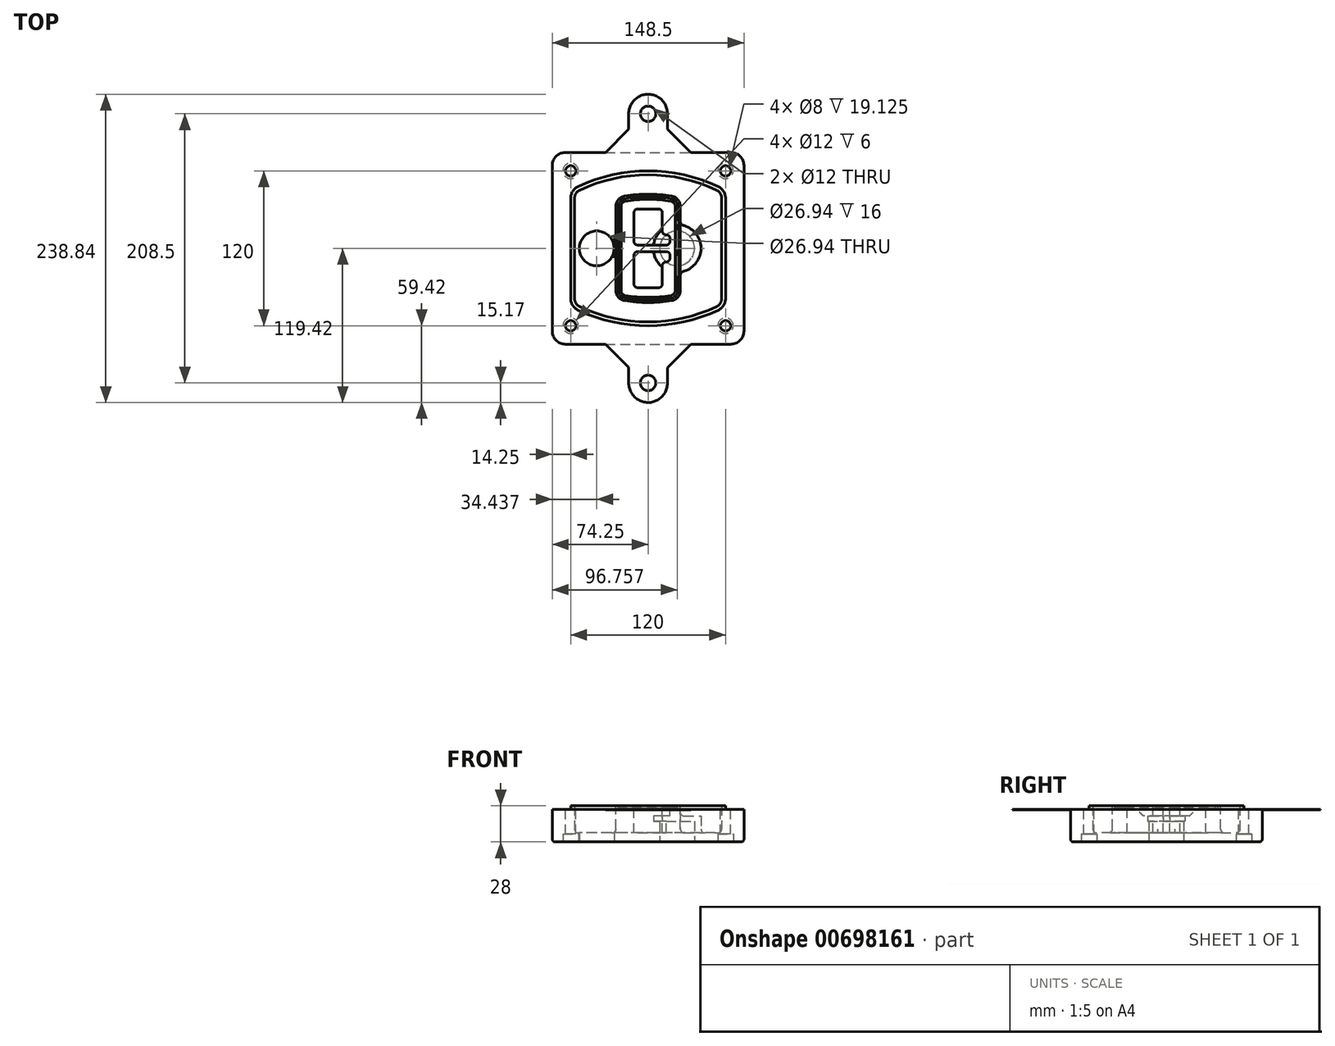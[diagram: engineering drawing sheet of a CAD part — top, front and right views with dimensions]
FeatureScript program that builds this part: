
annotation { "Feature Type Name" : "Feature", "Feature Type Description" : "" }
export const myFeature = defineFeature(function(context is Context, id is Id, definition is map)
    precondition{}
    {
        {
            var Q0;
            Q0=qCreatedBy(makeId("Top.planeOp"),FACE);
            var sketch = newSketch(context, id + "F0", { "sketchPlane" : qUnion([Q0])});
            skPoint(sketch, "E0.rect.middle", {"position": v(0, 0) * mm});
            skLineSegment(sketch, "E1.bottom", {"start": v(-64.25, -74.25) * mm, "end": v(64.25, -74.25) * mm});
            skLineSegment(sketch, "E1.top", {"start": v(-64.25, 74.25) * mm, "end": v(64.25, 74.25) * mm});
            skLineSegment(sketch, "E1.left", {"start": v(-74.25, -64.25) * mm, "end": v(-74.25, 64.25) * mm});
            skLineSegment(sketch, "E1.right", {"start": v(74.25, -64.25) * mm, "end": v(74.25, 64.25) * mm});
            skLineSegment(sketch, "E2", {"start": v(-74.25, 74.25) * mm, "end": v(74.25, -74.25) * mm, "construction": true});
            skLineSegment(sketch, "E3", {"start": v(74.25, 74.25) * mm, "end": v(-74.25, -74.25) * mm, "construction": true});
            skCircle(sketch, "E4", {"center": v(-60, 60) * mm, "radius": 4 * mm});
            skCircle(sketch, "E5", {"center": v(60, 60) * mm, "radius": 4 * mm});
            skCircle(sketch, "E6", {"center": v(60, -60) * mm, "radius": 4 * mm});
            skCircle(sketch, "E7", {"center": v(-60, -60) * mm, "radius": 4 * mm});
            skLineSegment(sketch, "E8", {"start": v(-60, 60) * mm, "end": v(60, 60) * mm, "construction": true});
            skLineSegment(sketch, "E9", {"start": v(60, 60) * mm, "end": v(60, -60) * mm, "construction": true});
            skLineSegment(sketch, "E10", {"start": v(60, -60) * mm, "end": v(-60, -60) * mm, "construction": true});
            skLineSegment(sketch, "E11", {"start": v(-60, -60) * mm, "end": v(-60, 60) * mm, "construction": true});
            skLineSegment(sketch, "E12", {"start": v(-60, 38.83) * mm, "end": v(-60, -38.83) * mm});
            skLineSegment(sketch, "E13", {"start": v(60, 38.83) * mm, "end": v(60, -38.83) * mm});
            skArc(sketch, "E14", {"start": v(54.26, 47.88) * mm, "mid": v(0, 60) * mm, "end": v(-54.26, 47.88) * mm});
            skArc(sketch, "E15", {"start": v(-54.26, -47.88) * mm, "mid": v(0, -60) * mm, "end": v(54.26, -47.88) * mm});
            skLineSegment(sketch, "E16", {"start": v(-60, 0) * mm, "end": v(60, 0) * mm, "construction": true});
            skPoint(sketch, "E17.visualSharp", {"position": v(-60, -45) * mm});
            skArc(sketch, "E17.filletArc", {"start": v(-60, -38.83) * mm, "mid": v(-58.44, -44.2) * mm, "end": v(-54.26, -47.88) * mm});
            skPoint(sketch, "E18.visualSharp", {"position": v(-60, 45) * mm});
            skArc(sketch, "E18.filletArc", {"start": v(-54.26, 47.88) * mm, "mid": v(-58.44, 44.2) * mm, "end": v(-60, 38.83) * mm});
            skPoint(sketch, "E19.visualSharp", {"position": v(60, 45) * mm});
            skArc(sketch, "E19.filletArc", {"start": v(60, 38.83) * mm, "mid": v(58.44, 44.2) * mm, "end": v(54.26, 47.88) * mm});
            skPoint(sketch, "E20.visualSharp", {"position": v(60, -45) * mm});
            skArc(sketch, "E20.filletArc", {"start": v(54.26, -47.88) * mm, "mid": v(58.44, -44.2) * mm, "end": v(60, -38.83) * mm});
            skPoint(sketch, "E21.visualSharp", {"position": v(-74.25, 74.25) * mm});
            skArc(sketch, "E21.filletArc", {"start": v(-64.25, 74.25) * mm, "mid": v(-71.32, 71.32) * mm, "end": v(-74.25, 64.25) * mm});
            skPoint(sketch, "E22.visualSharp", {"position": v(74.25, 74.25) * mm});
            skArc(sketch, "E22.filletArc", {"start": v(74.25, 64.25) * mm, "mid": v(71.32, 71.32) * mm, "end": v(64.25, 74.25) * mm});
            skPoint(sketch, "E23.visualSharp", {"position": v(74.25, -74.25) * mm});
            skArc(sketch, "E23.filletArc", {"start": v(64.25, -74.25) * mm, "mid": v(71.32, -71.32) * mm, "end": v(74.25, -64.25) * mm});
            skPoint(sketch, "E24.visualSharp", {"position": v(-74.25, -74.25) * mm});
            skArc(sketch, "E24.filletArc", {"start": v(-74.25, -64.25) * mm, "mid": v(-71.32, -71.32) * mm, "end": v(-64.25, -74.25) * mm});
            skArc(sketch, "E25.0", {"start": v(57, 38.83) * mm, "mid": v(55.9, 42.58) * mm, "end": v(52.98, 45.17) * mm});
            skLineSegment(sketch, "E25.1", {"start": v(57, 38.83) * mm, "end": v(57, -38.83) * mm});
            skArc(sketch, "E25.2", {"start": v(52.98, -45.17) * mm, "mid": v(55.9, -42.58) * mm, "end": v(57, -38.83) * mm});
            skArc(sketch, "E25.3", {"start": v(-52.98, -45.17) * mm, "mid": v(0, -57) * mm, "end": v(52.98, -45.17) * mm});
            skArc(sketch, "E25.4", {"start": v(-57, -38.83) * mm, "mid": v(-55.9, -42.58) * mm, "end": v(-52.98, -45.17) * mm});
            skArc(sketch, "E25.5", {"start": v(52.98, 45.17) * mm, "mid": v(0, 57) * mm, "end": v(-52.98, 45.17) * mm});
            skLineSegment(sketch, "E25.6", {"start": v(-57, 38.83) * mm, "end": v(-57, -38.83) * mm});
            skArc(sketch, "E25.7", {"start": v(-52.98, 45.17) * mm, "mid": v(-55.9, 42.58) * mm, "end": v(-57, 38.83) * mm});
            skArc(sketch, "E26.0", {"start": v(-55.96, 51.5) * mm, "mid": v(-61.82, 46.33) * mm, "end": v(-64, 38.83) * mm});
            skArc(sketch, "E26.1", {"start": v(55.96, 51.5) * mm, "mid": v(0, 64) * mm, "end": v(-55.96, 51.5) * mm});
            skArc(sketch, "E26.2", {"start": v(64, 38.83) * mm, "mid": v(61.82, 46.33) * mm, "end": v(55.96, 51.5) * mm});
            skLineSegment(sketch, "E26.3", {"start": v(64, 38.83) * mm, "end": v(64, -38.83) * mm});
            skArc(sketch, "E26.4", {"start": v(55.96, -51.5) * mm, "mid": v(61.82, -46.33) * mm, "end": v(64, -38.83) * mm});
            skLineSegment(sketch, "E26.5", {"start": v(-64, 38.83) * mm, "end": v(-64, -38.83) * mm});
            skArc(sketch, "E26.6", {"start": v(-55.96, -51.5) * mm, "mid": v(0, -64) * mm, "end": v(55.96, -51.5) * mm});
            skArc(sketch, "E26.7", {"start": v(-64, -38.83) * mm, "mid": v(-61.82, -46.33) * mm, "end": v(-55.96, -51.5) * mm});
            skSolve(sketch);
        }
        {
            var Q0;
            Q0=makeQuery(id+"F0.imprint","IMPRINT",FACE,{"disambiguationData":[TD([[makeQuery(id+"F0.imprint","IMPRINT",EDGE,{"derivedFrom":sQuery(id+"F0.wireOp",EDGE,"E1.bottom")}),1.0]])]});
            var Q1;
            Q1=makeQuery(id+"F0.imprint","IMPRINT",FACE,{"disambiguationData":[TD([[makeQuery(id+"F0.imprint","IMPRINT",EDGE,{"derivedFrom":sQuery(id+"F0.wireOp",EDGE,"E12")}),1.0]])]});
            var Q2;
            Q2=makeQuery(id+"F0.imprint","IMPRINT",FACE,{"disambiguationData":[TD([[makeQuery(id+"F0.imprint","IMPRINT",EDGE,{"derivedFrom":sQuery(id+"F0.wireOp",EDGE,"E25.0")}),1.0]])]});
            var Q3;
            Q3=makeQuery(id+"F0.imprint","IMPRINT",FACE,{"disambiguationData":[TD([[makeQuery(id+"F0.imprint","IMPRINT",EDGE,{"derivedFrom":sQuery(id+"F0.wireOp",EDGE,"E12")}),-1.0]])]});
            extrude(context, id + "F1", {"entities" : qUnion([Q0, Q1, Q2, Q3]), "oppositeDirection" : true, "depth" : 25 * mm});
        }
        {
            var Q0;
            Q0=makeQuery(id+"F0.imprint","IMPRINT",FACE,{"disambiguationData":[TD([[makeQuery(id+"F0.imprint","IMPRINT",EDGE,{"derivedFrom":sQuery(id+"F0.wireOp",EDGE,"E12")}),1.0]])]});
            extrude(context, id + "F2", {"entities" : qUnion([Q0]), "operationType" : NewBodyOperationType.ADD, "depth" : 3 * mm});
        }
        {
            var Q0;
            Q0=makeQuery(id+"F0.imprint","IMPRINT",FACE,{"disambiguationData":[TD([[makeQuery(id+"F0.imprint","IMPRINT",EDGE,{"derivedFrom":sQuery(id+"F0.wireOp",EDGE,"E25.0")}),1.0]])]});
            extrude(context, id + "F3", {"entities" : qUnion([Q0]), "operationType" : NewBodyOperationType.REMOVE, "oppositeDirection" : true, "depth" : 18 * mm});
        }
        {
            var Q0;
            Q0=makeQuery(id+"F2.opExtrude","CAP_FACE",FACE,{"disambiguationData":[OSD([sQuery(id+"F0.wireOp",EDGE,"E12"),sQuery(id+"F0.wireOp",EDGE,"E13"),sQuery(id+"F0.wireOp",EDGE,"E14"),sQuery(id+"F0.wireOp",EDGE,"E15"),sQuery(id+"F0.wireOp",EDGE,"E17.filletArc"),sQuery(id+"F0.wireOp",EDGE,"E18.filletArc"),sQuery(id+"F0.wireOp",EDGE,"E19.filletArc"),sQuery(id+"F0.wireOp",EDGE,"E20.filletArc"),sQuery(id+"F0.wireOp",EDGE,"E25.0"),sQuery(id+"F0.wireOp",EDGE,"E25.1"),sQuery(id+"F0.wireOp",EDGE,"E25.2"),sQuery(id+"F0.wireOp",EDGE,"E25.3"),sQuery(id+"F0.wireOp",EDGE,"E25.4"),sQuery(id+"F0.wireOp",EDGE,"E25.5"),sQuery(id+"F0.wireOp",EDGE,"E25.6"),sQuery(id+"F0.wireOp",EDGE,"E25.7")])],"isStart":false});
            var sketch = newSketch(context, id + "F4", { "sketchPlane" : qUnion([Q0])});
            skArc(sketch, "E27.0", {"start": v(-18.34, -40.45) * mm, "mid": v(0, -42) * mm, "end": v(18.34, -40.45) * mm});
            skArc(sketch, "E28.0", {"start": v(18.34, 40.45) * mm, "mid": v(0, 42) * mm, "end": v(-18.34, 40.45) * mm});
            skLineSegment(sketch, "E29", {"start": v(-25, 32.57) * mm, "end": v(-25, -32.57) * mm});
            skLineSegment(sketch, "E30", {"start": v(25, 32.57) * mm, "end": v(25, -32.57) * mm});
            skLineSegment(sketch, "E31", {"start": v(-25, 39.1) * mm, "end": v(25, 39.1) * mm, "construction": true});
            skLineSegment(sketch, "E32", {"start": v(-25, -39.1) * mm, "end": v(25, -39.1) * mm, "construction": true});
            skPoint(sketch, "E33.visualSharp", {"position": v(-25, 39.1) * mm});
            skArc(sketch, "E33.filletArc", {"start": v(-18.34, 40.45) * mm, "mid": v(-23.11, 37.73) * mm, "end": v(-25, 32.57) * mm});
            skPoint(sketch, "E34.visualSharp", {"position": v(25, 39.1) * mm});
            skArc(sketch, "E34.filletArc", {"start": v(25, 32.57) * mm, "mid": v(23.11, 37.73) * mm, "end": v(18.34, 40.45) * mm});
            skPoint(sketch, "E35.visualSharp", {"position": v(25, -39.1) * mm});
            skArc(sketch, "E35.filletArc", {"start": v(18.34, -40.45) * mm, "mid": v(23.11, -37.73) * mm, "end": v(25, -32.57) * mm});
            skPoint(sketch, "E36.visualSharp", {"position": v(-25, -39.1) * mm});
            skArc(sketch, "E36.filletArc", {"start": v(-25, -32.57) * mm, "mid": v(-23.11, -37.73) * mm, "end": v(-18.34, -40.45) * mm});
            skArc(sketch, "E37.0", {"start": v(52.98, 45.17) * mm, "mid": v(0, 57) * mm, "end": v(-52.98, 45.17) * mm});
            skArc(sketch, "E37.1", {"start": v(-52.98, 45.17) * mm, "mid": v(-55.9, 42.58) * mm, "end": v(-57, 38.83) * mm});
            skLineSegment(sketch, "E37.2", {"start": v(-57, 38.83) * mm, "end": v(-57, -38.83) * mm});
            skArc(sketch, "E37.3", {"start": v(-57, -38.83) * mm, "mid": v(-55.9, -42.58) * mm, "end": v(-52.98, -45.17) * mm});
            skArc(sketch, "E37.4", {"start": v(-52.98, -45.17) * mm, "mid": v(0, -57) * mm, "end": v(52.98, -45.17) * mm});
            skArc(sketch, "E37.5", {"start": v(52.98, -45.17) * mm, "mid": v(55.9, -42.58) * mm, "end": v(57, -38.83) * mm});
            skLineSegment(sketch, "E37.6", {"start": v(57, 38.83) * mm, "end": v(57, -38.83) * mm});
            skArc(sketch, "E37.7", {"start": v(57, 38.83) * mm, "mid": v(55.9, 42.58) * mm, "end": v(52.98, 45.17) * mm});
            skLineSegment(sketch, "E38.0", {"start": v(23, 32.57) * mm, "end": v(23, -32.57) * mm});
            skArc(sketch, "E38.1", {"start": v(18, -38.48) * mm, "mid": v(21.58, -36.44) * mm, "end": v(23, -32.57) * mm});
            skArc(sketch, "E38.2", {"start": v(-18, -38.48) * mm, "mid": v(0, -40) * mm, "end": v(18, -38.48) * mm});
            skArc(sketch, "E38.3", {"start": v(-23, -32.57) * mm, "mid": v(-21.58, -36.44) * mm, "end": v(-18, -38.48) * mm});
            skLineSegment(sketch, "E38.4", {"start": v(-23, 32.57) * mm, "end": v(-23, -32.57) * mm});
            skArc(sketch, "E38.5", {"start": v(23, 32.57) * mm, "mid": v(21.58, 36.44) * mm, "end": v(18, 38.48) * mm});
            skArc(sketch, "E38.6", {"start": v(-18, 38.48) * mm, "mid": v(-21.58, 36.44) * mm, "end": v(-23, 32.57) * mm});
            skArc(sketch, "E38.7", {"start": v(18, 38.48) * mm, "mid": v(0, 40) * mm, "end": v(-18, 38.48) * mm});
            skArc(sketch, "E39.0", {"start": v(21, 32.57) * mm, "mid": v(20.06, 35.15) * mm, "end": v(17.67, 36.5) * mm});
            skLineSegment(sketch, "E39.1", {"start": v(21, 32.57) * mm, "end": v(21, -32.57) * mm});
            skArc(sketch, "E39.2", {"start": v(17.67, -36.5) * mm, "mid": v(20.06, -35.15) * mm, "end": v(21, -32.57) * mm});
            skArc(sketch, "E39.3", {"start": v(-17.67, -36.5) * mm, "mid": v(0, -38) * mm, "end": v(17.67, -36.5) * mm});
            skArc(sketch, "E39.4", {"start": v(-21, -32.57) * mm, "mid": v(-20.06, -35.15) * mm, "end": v(-17.67, -36.5) * mm});
            skArc(sketch, "E39.5", {"start": v(17.67, 36.5) * mm, "mid": v(0, 38) * mm, "end": v(-17.67, 36.5) * mm});
            skLineSegment(sketch, "E39.6", {"start": v(-21, 32.57) * mm, "end": v(-21, -32.57) * mm});
            skArc(sketch, "E39.7", {"start": v(-17.67, 36.5) * mm, "mid": v(-20.06, 35.15) * mm, "end": v(-21, 32.57) * mm});
            skLineSegment(sketch, "E40", {"start": v(-25, 0) * mm, "end": v(25, 0) * mm, "construction": true});
            skLineSegment(sketch, "E41", {"start": v(-11, 5.5) * mm, "end": v(-11, 27.5) * mm});
            skLineSegment(sketch, "E42", {"start": v(-8, 30.5) * mm, "end": v(8, 30.5) * mm});
            skLineSegment(sketch, "E43", {"start": v(11, 27.5) * mm, "end": v(11, 13.5) * mm});
            skLineSegment(sketch, "E44", {"start": v(14, 10.5) * mm, "end": v(14, 10.5) * mm});
            skLineSegment(sketch, "E45", {"start": v(17, 7.5) * mm, "end": v(17, 5.5) * mm});
            skLineSegment(sketch, "E46", {"start": v(14, 2.5) * mm, "end": v(-8, 2.5) * mm});
            skPoint(sketch, "E47.visualSharp", {"position": v(-11, 30.5) * mm});
            skArc(sketch, "E47.filletArc", {"start": v(-8, 30.5) * mm, "mid": v(-10.12, 29.62) * mm, "end": v(-11, 27.5) * mm});
            skPoint(sketch, "E48.visualSharp", {"position": v(11, 30.5) * mm});
            skArc(sketch, "E48.filletArc", {"start": v(11, 27.5) * mm, "mid": v(10.12, 29.62) * mm, "end": v(8, 30.5) * mm});
            skPoint(sketch, "E49.visualSharp", {"position": v(11, 10.5) * mm});
            skArc(sketch, "E49.filletArc", {"start": v(11, 13.5) * mm, "mid": v(11.88, 11.38) * mm, "end": v(14, 10.5) * mm});
            skPoint(sketch, "E50.visualSharp", {"position": v(17, 10.5) * mm});
            skArc(sketch, "E50.filletArc", {"start": v(17, 7.5) * mm, "mid": v(16.12, 9.62) * mm, "end": v(14, 10.5) * mm});
            skPoint(sketch, "E51.visualSharp", {"position": v(17, 2.5) * mm});
            skArc(sketch, "E51.filletArc", {"start": v(14, 2.5) * mm, "mid": v(16.12, 3.38) * mm, "end": v(17, 5.5) * mm});
            skPoint(sketch, "E52.visualSharp", {"position": v(-11, 2.5) * mm});
            skArc(sketch, "E52.filletArc", {"start": v(-11, 5.5) * mm, "mid": v(-10.12, 3.38) * mm, "end": v(-8, 2.5) * mm});
            skLineSegment(sketch, "E53.0.MirrorCS", {"start": v(14, -2.5) * mm, "end": v(-8, -2.5) * mm});
            skArc(sketch, "E54.0.MirrorCS", {"start": v(-11, -5.5) * mm, "mid": v(-10.12, -3.38) * mm, "end": v(-8, -2.5) * mm});
            skLineSegment(sketch, "E55.0.MirrorCS", {"start": v(-11, -5.5) * mm, "end": v(-11, -27.5) * mm});
            skArc(sketch, "E56.0.MirrorCS", {"start": v(-8, -30.5) * mm, "mid": v(-10.12, -29.62) * mm, "end": v(-11, -27.5) * mm});
            skLineSegment(sketch, "E57.0.MirrorCS", {"start": v(-8, -30.5) * mm, "end": v(8, -30.5) * mm});
            skArc(sketch, "E58.0.MirrorCS", {"start": v(11, -27.5) * mm, "mid": v(10.12, -29.62) * mm, "end": v(8, -30.5) * mm});
            skLineSegment(sketch, "E59.0.MirrorCS", {"start": v(11, -27.5) * mm, "end": v(11, -13.5) * mm});
            skArc(sketch, "E60.0.MirrorCS", {"start": v(11, -13.5) * mm, "mid": v(11.88, -11.38) * mm, "end": v(14, -10.5) * mm});
            skArc(sketch, "E61.0.MirrorCS", {"start": v(17, -7.5) * mm, "mid": v(16.12, -9.62) * mm, "end": v(14, -10.5) * mm});
            skLineSegment(sketch, "E62.0.MirrorCS", {"start": v(17, -7.5) * mm, "end": v(17, -5.5) * mm});
            skArc(sketch, "E63.0.MirrorCS", {"start": v(14, -2.5) * mm, "mid": v(16.12, -3.38) * mm, "end": v(17, -5.5) * mm});
            skSolve(sketch);
        }
        {
            var Q0;
            Q0=makeQuery(id+"F4.imprint","IMPRINT",FACE,{"disambiguationData":[TD([[makeQuery(id+"F4.imprint","IMPRINT",EDGE,{"derivedFrom":sQuery(id+"F4.wireOp",EDGE,"E27.0")}),1.0]])]});
            var Q1;
            Q1=makeQuery(id+"F4.imprint","IMPRINT",FACE,{"disambiguationData":[TD([[makeQuery(id+"F4.imprint","IMPRINT",EDGE,{"derivedFrom":sQuery(id+"F4.wireOp",EDGE,"E38.0")}),-1.0]])]});
            var Q2;
            Q2=makeQuery(id+"F4.imprint","IMPRINT",FACE,{"disambiguationData":[TD([[makeQuery(id+"F4.imprint","IMPRINT",EDGE,{"derivedFrom":sQuery(id+"F4.wireOp",EDGE,"E39.0")}),1.0]])]});
            extrude(context, id + "F5", {"entities" : qUnion([Q0, Q1, Q2]), "operationType" : NewBodyOperationType.ADD, "endBound" : BoundingType.UP_TO_NEXT, "oppositeDirection" : true, "depth" : 25 * mm});
        }
        {
            var Q0;
            Q0=makeQuery(id+"F4.imprint","IMPRINT",FACE,{"disambiguationData":[TD([[makeQuery(id+"F4.imprint","IMPRINT",EDGE,{"derivedFrom":sQuery(id+"F4.wireOp",EDGE,"E38.0")}),-1.0]])]});
            extrude(context, id + "F6", {"entities" : qUnion([Q0]), "operationType" : NewBodyOperationType.REMOVE, "oppositeDirection" : true, "depth" : 2 * mm});
        }
        {
            var Q0;
            Q0=makeQuery(id+"F1.opExtrude","CAP_FACE",FACE,{"disambiguationData":[OSD([sQuery(id+"F0.wireOp",EDGE,"E1.bottom"),sQuery(id+"F0.wireOp",EDGE,"E1.top"),sQuery(id+"F0.wireOp",EDGE,"E1.left"),sQuery(id+"F0.wireOp",EDGE,"E1.right"),sQuery(id+"F0.wireOp",EDGE,"E4"),sQuery(id+"F0.wireOp",EDGE,"E5"),sQuery(id+"F0.wireOp",EDGE,"E6"),sQuery(id+"F0.wireOp",EDGE,"E7"),sQuery(id+"F0.wireOp",EDGE,"E21.filletArc"),sQuery(id+"F0.wireOp",EDGE,"E22.filletArc"),sQuery(id+"F0.wireOp",EDGE,"E23.filletArc"),sQuery(id+"F0.wireOp",EDGE,"E24.filletArc")])],"isStart":false});
            var sketch = newSketch(context, id + "F7", { "sketchPlane" : qUnion([Q0])});
            skCircle(sketch, "E64", {"center": v(22.5, 0) * mm, "radius": 13.47 * mm});
            skCircle(sketch, "E65", {"center": v(-39.81, 0) * mm, "radius": 13.47 * mm});
            skLineSegment(sketch, "E66", {"start": v(74.25, 0) * mm, "end": v(-74.25, 0) * mm});
            skCircle(sketch, "E67", {"center": v(22.5, 0) * mm, "radius": 18.47 * mm});
            skCircle(sketch, "E68", {"center": v(60, -60) * mm, "radius": 6 * mm});
            skCircle(sketch, "E69", {"center": v(-60, -60) * mm, "radius": 6 * mm});
            skCircle(sketch, "E70", {"center": v(-60, 60) * mm, "radius": 6 * mm});
            skCircle(sketch, "E71", {"center": v(60, 60) * mm, "radius": 6 * mm});
            skSolve(sketch);
        }
        {
            var Q0;
            {var subQ1=sQuery(id+"F7.wireOp",EDGE,"E66");var subQ4=sQuery(id+"F7.wireOp",EDGE,"E64");var subQ6=makeQuery(id+"F7.imprint","INTERSECT",VERTEX,{"disambiguationData":[OD(0.0)],"derivedFrom":[subQ4,subQ1]});Q0=makeQuery(id+"F7.imprint","IMPRINT",FACE,{"disambiguationData":[TD([[makeQuery(id+"F7.imprint","IMPRINT",EDGE,{"disambiguationData":[TD([[subQ6,-1.0]])],"derivedFrom":subQ4}),-1.0]])]});}
            var Q1;
            {var subQ0=sQuery(id+"F7.wireOp",EDGE,"E66");var subQ1=sQuery(id+"F7.wireOp",EDGE,"E64");var subQ3=makeQuery(id+"F7.imprint","INTERSECT",VERTEX,{"disambiguationData":[OD(0.0)],"derivedFrom":[subQ1,subQ0]});Q1=makeQuery(id+"F7.imprint","IMPRINT",FACE,{"disambiguationData":[TD([[makeQuery(id+"F7.imprint","IMPRINT",EDGE,{"disambiguationData":[TD([[subQ3,-1.0]])],"derivedFrom":subQ1}),1.0]])]});}
            var Q2;
            {var subQ0=sQuery(id+"F7.wireOp",EDGE,"E66");var subQ1=sQuery(id+"F7.wireOp",EDGE,"E64");var subQ3=makeQuery(id+"F7.imprint","INTERSECT",VERTEX,{"disambiguationData":[OD(0.0)],"derivedFrom":[subQ1,subQ0]});Q2=makeQuery(id+"F7.imprint","IMPRINT",FACE,{"disambiguationData":[TD([[makeQuery(id+"F7.imprint","IMPRINT",EDGE,{"disambiguationData":[TD([[subQ3,1.0]])],"derivedFrom":subQ1}),1.0]])]});}
            var Q3;
            {var subQ1=sQuery(id+"F7.wireOp",EDGE,"E66");var subQ4=sQuery(id+"F7.wireOp",EDGE,"E64");var subQ6=makeQuery(id+"F7.imprint","INTERSECT",VERTEX,{"disambiguationData":[OD(0.0)],"derivedFrom":[subQ4,subQ1]});Q3=makeQuery(id+"F7.imprint","IMPRINT",FACE,{"disambiguationData":[TD([[makeQuery(id+"F7.imprint","IMPRINT",EDGE,{"disambiguationData":[TD([[subQ6,1.0]])],"derivedFrom":subQ4}),-1.0]])]});}
            extrude(context, id + "F8", {"entities" : qUnion([Q0, Q1, Q2, Q3]), "operationType" : NewBodyOperationType.ADD, "oppositeDirection" : true, "depth" : 20 * mm});
        }
        {
            var Q0;
            {var subQ0=sQuery(id+"F7.wireOp",EDGE,"E66");var subQ1=sQuery(id+"F7.wireOp",EDGE,"E64");var subQ3=makeQuery(id+"F7.imprint","INTERSECT",VERTEX,{"disambiguationData":[OD(0.0)],"derivedFrom":[subQ1,subQ0]});Q0=makeQuery(id+"F7.imprint","IMPRINT",FACE,{"disambiguationData":[TD([[makeQuery(id+"F7.imprint","IMPRINT",EDGE,{"disambiguationData":[TD([[subQ3,-1.0]])],"derivedFrom":subQ1}),1.0]])]});}
            var Q1;
            {var subQ0=sQuery(id+"F7.wireOp",EDGE,"E66");var subQ1=sQuery(id+"F7.wireOp",EDGE,"E64");var subQ3=makeQuery(id+"F7.imprint","INTERSECT",VERTEX,{"disambiguationData":[OD(0.0)],"derivedFrom":[subQ1,subQ0]});Q1=makeQuery(id+"F7.imprint","IMPRINT",FACE,{"disambiguationData":[TD([[makeQuery(id+"F7.imprint","IMPRINT",EDGE,{"disambiguationData":[TD([[subQ3,1.0]])],"derivedFrom":subQ1}),1.0]])]});}
            extrude(context, id + "F9", {"entities" : qUnion([Q0, Q1]), "operationType" : NewBodyOperationType.REMOVE, "oppositeDirection" : true, "depth" : 16 * mm});
        }
        {
            var Q0;
            {var subQ0=sQuery(id+"F7.wireOp",EDGE,"E66");var subQ1=sQuery(id+"F7.wireOp",EDGE,"E65");var subQ3=makeQuery(id+"F7.imprint","INTERSECT",VERTEX,{"disambiguationData":[OD(0.0)],"derivedFrom":[subQ1,subQ0]});Q0=makeQuery(id+"F7.imprint","IMPRINT",FACE,{"disambiguationData":[TD([[makeQuery(id+"F7.imprint","IMPRINT",EDGE,{"disambiguationData":[TD([[subQ3,-1.0]])],"derivedFrom":subQ1}),1.0]])]});}
            var Q1;
            {var subQ0=sQuery(id+"F7.wireOp",EDGE,"E66");var subQ1=sQuery(id+"F7.wireOp",EDGE,"E65");var subQ3=makeQuery(id+"F7.imprint","INTERSECT",VERTEX,{"disambiguationData":[OD(0.0)],"derivedFrom":[subQ1,subQ0]});Q1=makeQuery(id+"F7.imprint","IMPRINT",FACE,{"disambiguationData":[TD([[makeQuery(id+"F7.imprint","IMPRINT",EDGE,{"disambiguationData":[TD([[subQ3,1.0]])],"derivedFrom":subQ1}),1.0]])]});}
            extrude(context, id + "F10", {"entities" : qUnion([Q0, Q1]), "operationType" : NewBodyOperationType.REMOVE, "oppositeDirection" : true, "depth" : 25 * mm});
        }
        {
            var Q0;
            Q0=makeQuery(id+"F7.imprint","IMPRINT",FACE,{"disambiguationData":[TD([[makeQuery(id+"F7.imprint","IMPRINT",EDGE,{"derivedFrom":sQuery(id+"F7.wireOp",EDGE,"E68")}),1.0]])]});
            var Q1;
            Q1=makeQuery(id+"F7.imprint","IMPRINT",FACE,{"disambiguationData":[TD([[makeQuery(id+"F7.imprint","IMPRINT",EDGE,{"derivedFrom":makeQuery(id+"F1.opExtrude","CAP_EDGE",EDGE,{"disambiguationData":[OSD([sQuery(id+"F0.wireOp",EDGE,"E5")])],"isStart":false})}),-1.0]])]});
            var Q2;
            Q2=makeQuery(id+"F7.imprint","IMPRINT",FACE,{"disambiguationData":[TD([[makeQuery(id+"F7.imprint","IMPRINT",EDGE,{"derivedFrom":sQuery(id+"F7.wireOp",EDGE,"E69")}),1.0]])]});
            var Q3;
            Q3=makeQuery(id+"F7.imprint","IMPRINT",FACE,{"disambiguationData":[TD([[makeQuery(id+"F7.imprint","IMPRINT",EDGE,{"derivedFrom":makeQuery(id+"F1.opExtrude","CAP_EDGE",EDGE,{"disambiguationData":[OSD([sQuery(id+"F0.wireOp",EDGE,"E4")])],"isStart":false})}),-1.0]])]});
            var Q4;
            Q4=makeQuery(id+"F7.imprint","IMPRINT",FACE,{"disambiguationData":[TD([[makeQuery(id+"F7.imprint","IMPRINT",EDGE,{"derivedFrom":sQuery(id+"F7.wireOp",EDGE,"E70")}),1.0]])]});
            var Q5;
            Q5=makeQuery(id+"F7.imprint","IMPRINT",FACE,{"disambiguationData":[TD([[makeQuery(id+"F7.imprint","IMPRINT",EDGE,{"derivedFrom":makeQuery(id+"F1.opExtrude","CAP_EDGE",EDGE,{"disambiguationData":[OSD([sQuery(id+"F0.wireOp",EDGE,"E7")])],"isStart":false})}),-1.0]])]});
            var Q6;
            Q6=makeQuery(id+"F7.imprint","IMPRINT",FACE,{"disambiguationData":[TD([[makeQuery(id+"F7.imprint","IMPRINT",EDGE,{"derivedFrom":sQuery(id+"F7.wireOp",EDGE,"E71")}),1.0]])]});
            var Q7;
            Q7=makeQuery(id+"F7.imprint","IMPRINT",FACE,{"disambiguationData":[TD([[makeQuery(id+"F7.imprint","IMPRINT",EDGE,{"derivedFrom":makeQuery(id+"F1.opExtrude","CAP_EDGE",EDGE,{"disambiguationData":[OSD([sQuery(id+"F0.wireOp",EDGE,"E6")])],"isStart":false})}),-1.0]])]});
            extrude(context, id + "F11", {"entities" : qUnion([Q0, Q1, Q2, Q3, Q4, Q5, Q6, Q7]), "operationType" : NewBodyOperationType.REMOVE, "oppositeDirection" : true, "depth" : 6 * mm});
        }
        {
            var Q0;
            Q0=makeQuery(id+"F9.boolean.opBoolean","COPY",FACE,{"derivedFrom":makeQuery(id+"F9.opExtrude","CAP_FACE",FACE,{"disambiguationData":[OSD([sQuery(id+"F7.wireOp",EDGE,"E64")])],"isStart":false})});
            var sketch = newSketch(context, id + "F12", { "sketchPlane" : qUnion([Q0])});
            skArc(sketch, "E72.0", {"start": v(11, 14.45) * mm, "mid": v(6.45, 9.13) * mm, "end": v(4.2, 2.5) * mm});
            skArc(sketch, "E72.1", {"start": v(4.2, -2.5) * mm, "mid": v(6.45, -9.13) * mm, "end": v(11, -14.45) * mm});
            skLineSegment(sketch, "E73", {"start": v(4.2, -2.5) * mm, "end": v(14, -2.5) * mm});
            skLineSegment(sketch, "E74.0", {"start": v(14, 2.5) * mm, "end": v(4.2, 2.5) * mm});
            skArc(sketch, "E74.1", {"start": v(14, 2.5) * mm, "mid": v(16.12, 3.38) * mm, "end": v(17, 5.5) * mm});
            skLineSegment(sketch, "E74.2", {"start": v(17, 7.5) * mm, "end": v(17, 5.5) * mm});
            skArc(sketch, "E74.3", {"start": v(17, 7.5) * mm, "mid": v(16.12, 9.62) * mm, "end": v(14, 10.5) * mm});
            skArc(sketch, "E74.4", {"start": v(11, 13.5) * mm, "mid": v(11.88, 11.38) * mm, "end": v(14, 10.5) * mm});
            skLineSegment(sketch, "E74.5", {"start": v(11, 14.45) * mm, "end": v(11, 13.5) * mm});
            skLineSegment(sketch, "E74.7", {"start": v(14, -2.5) * mm, "end": v(4.2, -2.5) * mm});
            skArc(sketch, "E74.8", {"start": v(14, -2.5) * mm, "mid": v(16.12, -3.38) * mm, "end": v(17, -5.5) * mm});
            skLineSegment(sketch, "E74.9", {"start": v(17, -7.5) * mm, "end": v(17, -5.5) * mm});
            skArc(sketch, "E74.10", {"start": v(17, -7.5) * mm, "mid": v(16.12, -9.62) * mm, "end": v(14, -10.5) * mm});
            skArc(sketch, "E74.11", {"start": v(11, -13.5) * mm, "mid": v(11.88, -11.38) * mm, "end": v(14, -10.5) * mm});
            skLineSegment(sketch, "E74.12", {"start": v(11, -14.45) * mm, "end": v(11, -13.5) * mm});
            skPoint(sketch, "E75.orphan", {"position": v(11, -27.5) * mm});
            skPoint(sketch, "E76.orphan", {"position": v(-8, -2.5) * mm});
            skPoint(sketch, "E77.orphan", {"position": v(-8, 2.5) * mm});
            skPoint(sketch, "E78.orphan", {"position": v(11, 27.5) * mm});
            skSolve(sketch);
        }
        {
            var Q0;
            {var subQ7=sQuery(id+"F12.wireOp",EDGE,"E72.0");var subQ14=sQuery(id+"F12.wireOp",EDGE,"E72.1");var subQ16=sQuery(id+"F12.wireOp",EDGE,"E74.1");var subQ18=sQuery(id+"F12.wireOp",EDGE,"E74.8");Q0=qUnion([makeQuery(id+"F12.imprint","IMPRINT",FACE,{"disambiguationData":[TD([[makeQuery(id+"F12.imprint","IMPRINT",EDGE,{"derivedFrom":subQ7}),1.0]])]}),makeQuery(id+"F12.imprint","IMPRINT",FACE,{"disambiguationData":[TD([[makeQuery(id+"F12.imprint","IMPRINT",EDGE,{"derivedFrom":subQ14}),1.0]])]}),makeQuery(id+"F12.imprint","IMPRINT",FACE,{"disambiguationData":[TD([[makeQuery(id+"F12.imprint","IMPRINT",EDGE,{"derivedFrom":subQ16}),1.0]])]}),makeQuery(id+"F12.imprint","IMPRINT",FACE,{"disambiguationData":[TD([[makeQuery(id+"F12.imprint","IMPRINT",EDGE,{"derivedFrom":subQ18}),-1.0]])]})]);}
            var Q1;
            Q1=makeQuery(id+"F5.boolean.opBoolean","SPLIT",FACE,{"disambiguationData":[TD([makeQuery(id+"F5.opExtrude","SWEPT_FACE",FACE,{"disambiguationData":[OSD([sQuery(id+"F4.wireOp",EDGE,"E41")])]})])],"derivedFrom":makeQuery(id+"F3.boolean.opBoolean","COPY",FACE,{"derivedFrom":makeQuery(id+"F3.opExtrude","CAP_FACE",FACE,{"disambiguationData":[OSD([sQuery(id+"F0.wireOp",EDGE,"E25.0"),sQuery(id+"F0.wireOp",EDGE,"E25.1"),sQuery(id+"F0.wireOp",EDGE,"E25.2"),sQuery(id+"F0.wireOp",EDGE,"E25.3"),sQuery(id+"F0.wireOp",EDGE,"E25.4"),sQuery(id+"F0.wireOp",EDGE,"E25.5"),sQuery(id+"F0.wireOp",EDGE,"E25.6"),sQuery(id+"F0.wireOp",EDGE,"E25.7")])],"isStart":false})})});
            extrude(context, id + "F13", {"entities" : qUnion([Q0]), "operationType" : NewBodyOperationType.REMOVE, "endBound" : BoundingType.UP_TO_SURFACE, "endBoundEntityFace" : qUnion([Q1]), "depth" : 25 * mm});
        }
        {
            var Q0;
            Q0=makeQuery(id+"F3.boolean.opBoolean","COPY",EDGE,{"derivedFrom":makeQuery(id+"F3.opExtrude","CAP_EDGE",EDGE,{"disambiguationData":[OSD([sQuery(id+"F0.wireOp",EDGE,"E25.6")])],"isStart":false})});
            var Q1;
            Q1=makeQuery(id+"F8.boolean.opBoolean","INTERSECT",EDGE,{"derivedFrom":[makeQuery(id+"F5.opExtrude","SWEPT_FACE",FACE,{"disambiguationData":[OSD([sQuery(id+"F4.wireOp",EDGE,"E30")])]}),makeQuery(id+"F8.opExtrude","CAP_FACE",FACE,{"disambiguationData":[OSD([sQuery(id+"F7.wireOp",EDGE,"E67")])],"isStart":false})]});
            var Q2;
            Q2=makeQuery(id+"F8.boolean.opBoolean","INTERSECT",EDGE,{"disambiguationData":[OD(1.0)],"derivedFrom":[makeQuery(id+"F5.opExtrude","SWEPT_FACE",FACE,{"disambiguationData":[OSD([sQuery(id+"F4.wireOp",EDGE,"E30")])]}),makeQuery(id+"F8.opExtrude","SWEPT_FACE",FACE,{"disambiguationData":[OSD([sQuery(id+"F7.wireOp",EDGE,"E67")])]})]});
            var Q3;
            {var subQ0=sQuery(id+"F4.wireOp",EDGE,"E30");Q3=makeQuery(id+"F8.boolean.opBoolean","SPLIT",EDGE,{"disambiguationData":[TD([makeQuery(id+"F5.opExtrude","SWEPT_FACE",FACE,{"disambiguationData":[OSD([sQuery(id+"F4.wireOp",EDGE,"E35.filletArc")])]})])],"derivedFrom":makeQuery(id+"F5.opExtrude","CAP_EDGE",EDGE,{"disambiguationData":[OSD([subQ0])],"isStart":false})});}
            var Q4;
            {var subQ0=sQuery(id+"F0.wireOp",EDGE,"E25.7");var subQ1=sQuery(id+"F0.wireOp",EDGE,"E25.1");var subQ2=sQuery(id+"F0.wireOp",EDGE,"E25.6");var subQ3=sQuery(id+"F0.wireOp",EDGE,"E25.5");var subQ4=sQuery(id+"F0.wireOp",EDGE,"E25.4");var subQ5=sQuery(id+"F0.wireOp",EDGE,"E25.0");var subQ6=sQuery(id+"F0.wireOp",EDGE,"E25.2");var subQ7=sQuery(id+"F0.wireOp",EDGE,"E25.3");Q4=makeQuery(id+"F8.boolean.opBoolean","INTERSECT",EDGE,{"derivedFrom":[makeQuery(id+"F5.boolean.opBoolean","SPLIT",FACE,{"disambiguationData":[TD([makeQuery(id+"F2.opExtrude","SWEPT_FACE",FACE,{"disambiguationData":[OSD([subQ5])]})])],"derivedFrom":makeQuery(id+"F3.boolean.opBoolean","COPY",FACE,{"derivedFrom":makeQuery(id+"F3.opExtrude","CAP_FACE",FACE,{"disambiguationData":[OSD([subQ5,subQ1,subQ6,subQ7,subQ4,subQ3,subQ2,subQ0])],"isStart":false})})}),makeQuery(id+"F8.opExtrude","SWEPT_FACE",FACE,{"disambiguationData":[OSD([sQuery(id+"F7.wireOp",EDGE,"E67")])]})]});}
            var Q5;
            Q5=makeQuery(id+"F8.boolean.opBoolean","INTERSECT",EDGE,{"disambiguationData":[OD(0.0)],"derivedFrom":[makeQuery(id+"F5.opExtrude","SWEPT_FACE",FACE,{"disambiguationData":[OSD([sQuery(id+"F4.wireOp",EDGE,"E30")])]}),makeQuery(id+"F8.opExtrude","SWEPT_FACE",FACE,{"disambiguationData":[OSD([sQuery(id+"F7.wireOp",EDGE,"E67")])]})]});
            fillet(context, id + "F14", {"entities" : qUnion([Q0, Q1, Q2, Q3, Q4, Q5]), "radius" : 3 * mm, "tangentPropagation" : true, "allowEdgeOverflow" : false});
        }
        {
            var Q0;
            Q0=makeQuery(id+"F1.opExtrude","CAP_EDGE",EDGE,{"disambiguationData":[OSD([sQuery(id+"F0.wireOp",EDGE,"E1.bottom")])],"isStart":false});
            fillet(context, id + "F15", {"entities" : qUnion([Q0]), "radius" : 2 * mm, "tangentPropagation" : true, "allowEdgeOverflow" : false});
        }
        {
            var Q0;
            {var subQ0=sQuery(id+"F0.wireOp",EDGE,"E21.filletArc");var subQ1=sQuery(id+"F0.wireOp",EDGE,"E7");var subQ2=sQuery(id+"F0.wireOp",EDGE,"E6");var subQ3=sQuery(id+"F0.wireOp",EDGE,"E5");var subQ4=sQuery(id+"F0.wireOp",EDGE,"E4");var subQ5=sQuery(id+"F0.wireOp",EDGE,"E22.filletArc");var subQ6=sQuery(id+"F0.wireOp",EDGE,"E1.bottom");var subQ7=sQuery(id+"F0.wireOp",EDGE,"E1.right");var subQ8=sQuery(id+"F0.wireOp",EDGE,"E1.top");var subQ9=sQuery(id+"F0.wireOp",EDGE,"E1.left");var subQ10=sQuery(id+"F0.wireOp",EDGE,"E23.filletArc");var subQ11=sQuery(id+"F0.wireOp",EDGE,"E24.filletArc");Q0=makeQuery(id+"F2.boolean.opBoolean","SPLIT",FACE,{"disambiguationData":[TD([makeQuery(id+"F1.opExtrude","SWEPT_FACE",FACE,{"disambiguationData":[OSD([subQ6])]})])],"derivedFrom":makeQuery(id+"F1.opExtrude","CAP_FACE",FACE,{"disambiguationData":[OSD([subQ6,subQ8,subQ9,subQ7,subQ4,subQ3,subQ2,subQ1,subQ0,subQ5,subQ10,subQ11])],"isStart":true})});}
            var sketch = newSketch(context, id + "F16", { "sketchPlane" : qUnion([Q0])});
            skLineSegment(sketch, "E79", {"start": v(0, 104.25) * mm, "end": v(0, 74.25) * mm, "construction": true});
            skCircle(sketch, "E80", {"center": v(0, 104.25) * mm, "radius": 6 * mm});
            skLineSegment(sketch, "E81", {"start": v(33.17, 74.25) * mm, "end": v(15, 92.42) * mm});
            skLineSegment(sketch, "E82", {"start": v(15, 92.42) * mm, "end": v(15, 104.42) * mm});
            skLineSegment(sketch, "E83", {"start": v(-33, 74.25) * mm, "end": v(-15, 92.25) * mm});
            skLineSegment(sketch, "E84", {"start": v(-15, 92.25) * mm, "end": v(-15, 104.25) * mm});
            skArc(sketch, "E85", {"start": v(15, 104.42) * mm, "mid": v(-0.08, 119.41) * mm, "end": v(-15, 104.25) * mm});
            skLineSegment(sketch, "E86", {"start": v(74.25, 0) * mm, "end": v(-74.25, 0) * mm, "construction": true});
            skLineSegment(sketch, "E87.MirrorCS", {"start": v(-15, -92.25) * mm, "end": v(-15, -104.25) * mm});
            skArc(sketch, "E88.MirrorCS", {"start": v(15, -104.42) * mm, "mid": v(-0.08, -119.41) * mm, "end": v(-15, -104.25) * mm});
            skLineSegment(sketch, "E89.MirrorCS", {"start": v(15, -92.42) * mm, "end": v(15, -104.42) * mm});
            skLineSegment(sketch, "E90.MirrorCS", {"start": v(33.17, -74.25) * mm, "end": v(15, -92.42) * mm});
            skLineSegment(sketch, "E91.MirrorCS", {"start": v(-33, -74.25) * mm, "end": v(-15, -92.25) * mm});
            skCircle(sketch, "E92.MirrorC", {"center": v(0, -104.25) * mm, "radius": 6 * mm});
            skLineSegment(sketch, "E93.MirrorCS", {"start": v(0, -104.25) * mm, "end": v(0, -74.25) * mm, "construction": true});
            skSolve(sketch);
        }
        {
            var Q0;
            Q0=makeQuery(id+"F16.imprint","IMPRINT",FACE,{"disambiguationData":[TD([[makeQuery(id+"F16.imprint","IMPRINT",EDGE,{"derivedFrom":sQuery(id+"F16.wireOp",EDGE,"E87.MirrorCS")}),1.0]])]});
            var Q1;
            Q1=makeQuery(id+"F16.imprint","IMPRINT",FACE,{"disambiguationData":[TD([[makeQuery(id+"F16.imprint","IMPRINT",EDGE,{"derivedFrom":sQuery(id+"F16.wireOp",EDGE,"E80")}),-1.0]])]});
            var Q2;
            Q2=makeQuery(id+"F16.imprint","IMPRINT",FACE,{"disambiguationData":[TD([[makeQuery(id+"F16.imprint","IMPRINT",EDGE,{"derivedFrom":makeQuery(id+"F1.opExtrude","CAP_EDGE",EDGE,{"disambiguationData":[OSD([sQuery(id+"F0.wireOp",EDGE,"E1.left")])],"isStart":true})}),-1.0]])]});
            var Q3;
            Q3 = qSketchRegion(id + "F65GMHBdRBNsfed_1", true);
            extrude(context, id + "F17", {"entities" : qUnion([Q0, Q1, Q2, Q3]), "operationType" : NewBodyOperationType.ADD, "depth" : .125 * mm, "offsetDistance" : 25.4 * mm});
        }
    });
